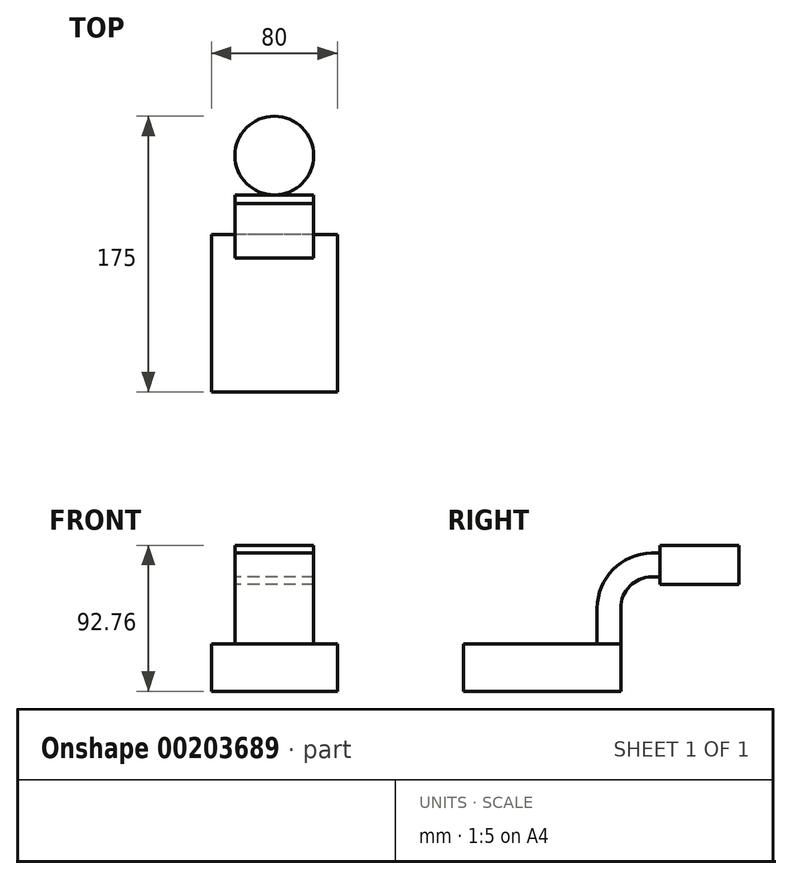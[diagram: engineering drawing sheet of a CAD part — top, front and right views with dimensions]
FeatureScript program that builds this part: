
annotation { "Feature Type Name" : "Feature", "Feature Type Description" : "" }
export const myFeature = defineFeature(function(context is Context, id is Id, definition is map)
    precondition{}
    {
        {
            var Q0;
            Q0=qCreatedBy(makeId("Right.planeOp"),FACE);
            var sketch = newSketch(context, id + "F0", { "sketchPlane" : qUnion([Q0])});
            skLineSegment(sketch, "E0.bottom", {"start": v(50, -15) * mm, "end": v(-50, -15) * mm});
            skLineSegment(sketch, "E0.top", {"start": v(50, 15) * mm, "end": v(-50, 15) * mm});
            skLineSegment(sketch, "E0.left", {"start": v(50, -15) * mm, "end": v(50, 15) * mm});
            skLineSegment(sketch, "E0.right", {"start": v(-50, -15) * mm, "end": v(-50, 15) * mm});
            skPoint(sketch, "E0.middle", {"position": v(0, 0) * mm});
            skLineSegment(sketch, "E1.bottom", {"start": v(75, 52.76) * mm, "end": v(125, 52.76) * mm});
            skLineSegment(sketch, "E1.top", {"start": v(75, 77.76) * mm, "end": v(125, 77.76) * mm});
            skLineSegment(sketch, "E1.left", {"start": v(75, 52.76) * mm, "end": v(75, 77.76) * mm});
            skLineSegment(sketch, "E1.right", {"start": v(125, 52.76) * mm, "end": v(125, 77.76) * mm});
            skPoint(sketch, "E1.middle", {"position": v(100, 65.26) * mm});
            skLineSegment(sketch, "E2", {"start": v(50, 15) * mm, "end": v(50, 37.76) * mm});
            skLineSegment(sketch, "E3", {"start": v(69.55, 57.76) * mm, "end": v(100, 57.76) * mm});
            skArc(sketch, "E4", {"start": v(50, 37.76) * mm, "mid": v(55.7, 51.75) * mm, "end": v(69.55, 57.76) * mm});
            skLineSegment(sketch, "E5.0", {"start": v(69.4, 72.76) * mm, "end": v(100, 72.76) * mm});
            skArc(sketch, "E5.1", {"start": v(35, 37.76) * mm, "mid": v(45.04, 62.3) * mm, "end": v(69.4, 72.76) * mm});
            skLineSegment(sketch, "E5.2", {"start": v(35, 15) * mm, "end": v(35, 37.76) * mm});
            skLineSegment(sketch, "E6", {"start": v(100, 77.76) * mm, "end": v(100, 52.76) * mm});
            skLineSegment(sketch, "E7", {"start": v(100, 72.76) * mm, "end": v(100, 57.76) * mm});
            skFitSpline(sketch, "E8", {"points": [v(-50, 15) * mm, v(69.4, 72.76) * mm], "startDerivative": vector(-2.4, 110.53) * mm, "endDerivative": vector(154.45, 2.24) * mm});
            skSolve(sketch);
        }
        {
            var Q0;
            Q0=makeQuery(id+"F0.imprint","IMPRINT",FACE,{"disambiguationData":[TD([[makeQuery(id+"F0.imprint","IMPRINT",EDGE,{"derivedFrom":sQuery(id+"F0.wireOp",EDGE,"E0.bottom")}),-1.0]])]});
            extrude(context, id + "F1", {"entities" : qUnion([Q0]), "endBound" : BoundingType.SYMMETRIC, "depth" : 80 * mm});
        }
        {
            var Q0;
            Q0=makeQuery(id+"F0.imprint","IMPRINT",FACE,{"disambiguationData":[TD([[makeQuery(id+"F0.imprint","IMPRINT",EDGE,{"derivedFrom":sQuery(id+"F0.wireOp",EDGE,"E5.1")}),1.0]])]});
            var Q1;
            {var subQ4=sQuery(id+"F0.wireOp",EDGE,"E2");Q1=makeQuery(id+"F0.imprint","IMPRINT",FACE,{"disambiguationData":[TD([[makeQuery(id+"F0.imprint","IMPRINT",EDGE,{"derivedFrom":subQ4}),1.0]])]});}
            var Q2;
            {var subQ5=sQuery(id+"F0.wireOp",EDGE,"E7");Q2=makeQuery(id+"F0.imprint","IMPRINT",FACE,{"disambiguationData":[TD([[makeQuery(id+"F0.imprint","IMPRINT",EDGE,{"derivedFrom":subQ5}),-1.0]])]});}
            extrude(context, id + "F2", {"entities" : qUnion([Q0, Q1, Q2]), "operationType" : NewBodyOperationType.ADD, "endBound" : BoundingType.SYMMETRIC, "depth" : 50 * mm});
        }
        {
            var Q0;
            {var subQ0=sQuery(id+"F0.wireOp",EDGE,"E1.right");Q0=makeQuery(id+"F0.imprint","IMPRINT",FACE,{"disambiguationData":[TD([[makeQuery(id+"F0.imprint","IMPRINT",EDGE,{"derivedFrom":subQ0}),1.0]])]});}
            var Q1;
            Q1=sQuery(id+"F0.wireOp",EDGE,"E6");
            revolve(context, id + "F3", {"operationType" : NewBodyOperationType.ADD, "entities" : qUnion([Q0]), "axis" : qUnion([Q1]), "revolveType" : RevolveType.FULL});
        }
    });
